# Revit family: Caroma Caravelle 550 Wall Basin
name_source: partatom
category: Plumbing Fixtures
revit_build: Autodesk Revit Architecture 2012 (Build: 20110309_2315)
units: mm (PartAtom-declared; Revit-internal decimal feet)

## types (6) — shared parameters
CW Connection = No
Default Elevation = 785 mm
Description = Caravelle Wall Basin
HW Connection = No
Manufacturer = Caroma
PlumbingMaterial_ANZRS = Porcelain-White-Caroma
Type Comments = Vitreous China Wall Basin
URL = www.caroma.com.au
Vent Connection = No
Waste = Metal-Chrome-Caroma
Waste Connection = Yes

## per-type parameters (varying)
| type | 1 Taphole | 3 Tapholes | Model | Pedestal | Shroud | Spout Penetration | Tap Penetrations |
| Caravelle - 3 Tap Holes with Shroud | No | Yes | 639030 | No | Yes | 0 mm  [stored 0 ft] | 0 mm  [stored 0 ft] |
| Caravelle - 1 Tap Hole with Shroud | Yes | No | 639010 | No | Yes | 0 mm  [stored 0 ft] | 100 mm  [stored 0.328084 ft] |
| Caravelle - 0 Tap Holes with Shroud | No | No | 639000 | No | Yes | 100 mm  [stored 0.328084 ft] | 100 mm  [stored 0.328084 ft] |
| Caravelle - 3 Tap Holes with Pedestal | No | Yes | 639030 | Yes | No | 0 mm  [stored 0 ft] | 0 mm  [stored 0 ft] |
| Caravelle - 1 Tap Hole with Pedestal | Yes | No | 639010 | Yes | No | 0 mm  [stored 0 ft] | 100 mm  [stored 0.328084 ft] |
| Caravelle - 0 Tap Holes with Pedestal | No | No | 639000 | Yes | No | 100 mm  [stored 0.328084 ft] | 100 mm  [stored 0.328084 ft] |

note: [stored X ft] marks values corroborated as IEEE doubles in the binary element streams (Revit-internal decimal feet)

## geometry (parser evidence)
native form markers: Blend x8, Sweep x8
no freeform markers — native parametric forms only
